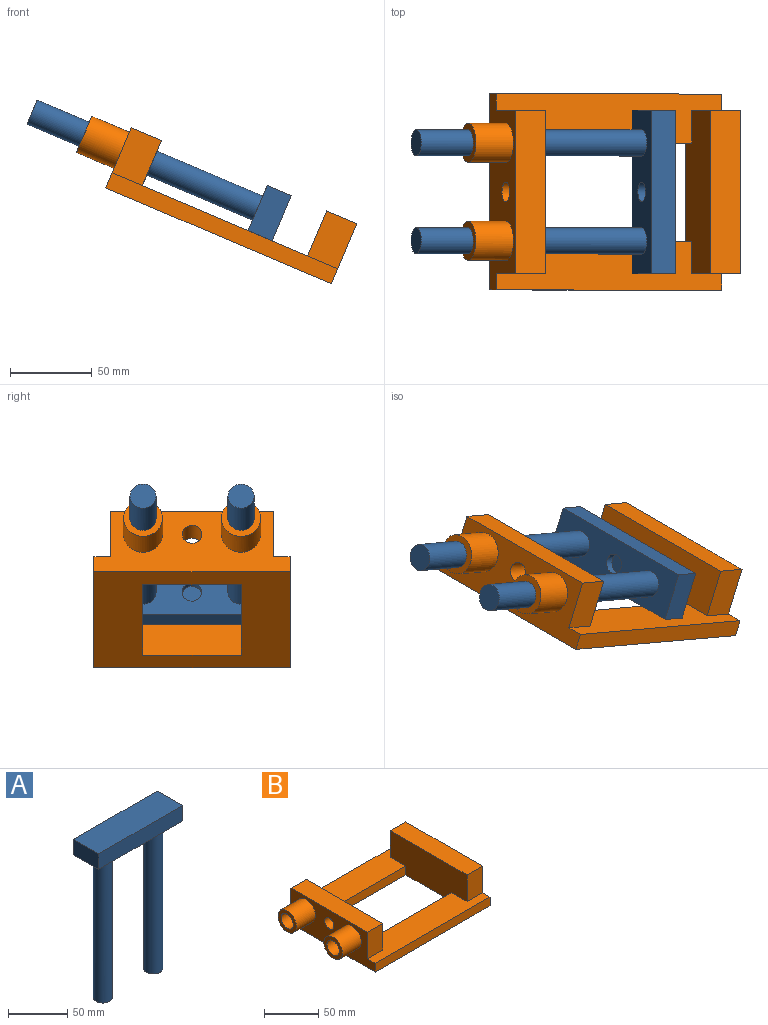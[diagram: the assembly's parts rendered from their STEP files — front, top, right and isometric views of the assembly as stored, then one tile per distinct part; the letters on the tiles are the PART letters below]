
ASSEMBLY  parts=2 mates=1
PART A: 12 faces, bbox 100x30x166 mm
  f0: plane 30x16mm, normal (1,0,0), area 480mm2, adj f1,f3,f4,f5
  f1: plane 100x16mm, normal (0,1,0), area 1600mm2, adj f0,f2,f4,f5
  f2: plane 30x16mm, normal (-1,0,0), area 480mm2, adj f1,f3,f4,f5
  f3: plane 100x16mm, normal (0,-1,0), area 1600mm2, adj f0,f2,f4,f5
  f4: plane 100x30mm, normal (0,0,1), area 3000mm2, adj f0,f1,f2,f3
  f5: plane 100x30mm, normal (0,0,-1), area 2484.8mm2, adj f0,f1,f2,f3,f6,f8,f10
  f6: cylinder r=8mm len=150mm, axis (0,0,1), area 7539.8mm2, adj f5,f7
  f7: plane 16x16mm, normal (0,0,-1), area 201.1mm2, adj f6
  f8: cylinder r=8mm len=150mm, axis (0,0,1), area 7539.8mm2, adj f5,f9
  f9: plane 16x16mm, normal (0,0,-1), area 201.1mm2, adj f8
  f10: cylinder r=6mm len=12mm, axis (0,0,-1), area 188.5mm2, adj f5,f11
  f11: plane 12x12mm, normal (0,0,-1), area 113.1mm2, adj f10
PART B: 24 faces, bbox 175x120x40 mm
  f0: plane 150x30mm, normal (0,0,1), area 3700mm2, adj f2,f3,f5,f6,f7,f9,f11,f15
  f1: plane 150x30mm, normal (0,0,1), area 3700mm2, adj f3,f4,f5,f7,f8,f9,f12,f14
  f2: plane 110x10mm, normal (0,-1,0), area 1100mm2, adj f0,f3,f9,f10
  f3: plane 100x40mm, normal (-1,0,0), area 3600mm2, adj f0,f1,f2,f4,f10,f11,f12,f13
  f4: plane 110x10mm, normal (0,1,0), area 1100mm2, adj f1,f3,f9,f10
  f5: plane 120x40mm, normal (1,0,0), area 4200mm2, adj f0,f1,f6,f8,f10,f11,f12,f13
  f6: plane 150x10mm, normal (0,1,0), area 1500mm2, adj f0,f5,f7,f10
  f7: plane 120x40mm, normal (-1,0,0), area 3182.1mm2, adj f0,f1,f6,f8,f10,f14,f15,f16
  f8: plane 150x10mm, normal (0,-1,0), area 1500mm2, adj f1,f5,f7,f10
  f9: plane 100x40mm, normal (1,0,0), area 3084.8mm2, adj f0,f1,f2,f4,f10,f14,f15,f16
  f10: plane 150x120mm, normal (0,0,-1), area 11400mm2, adj f2,f3,f4,f5,f6,f7,f8,f9
  f11: plane 30x20mm, normal (0,1,0), area 600mm2, adj f0,f3,f5,f13
  f12: plane 30x20mm, normal (0,-1,0), area 600mm2, adj f1,f3,f5,f13
  f13: plane 100x20mm, normal (0,0,1), area 2000mm2, adj f3,f5,f11,f12
  f14: plane 30x20mm, normal (0,-1,0), area 600mm2, adj f1,f7,f9,f16
  f15: plane 30x20mm, normal (0,1,0), area 600mm2, adj f0,f7,f9,f16
  f16: plane 100x20mm, normal (0,0,1), area 2000mm2, adj f7,f9,f14,f15
  f17: cylinder r=6mm len=20mm, axis (-1,0,0), area 754mm2, adj f7,f9
  f18: cylinder r=12mm len=25mm, axis (1,0,0), area 1885mm2, adj f7,f19
  f19: plane 24x24mm, normal (-1,0,0), area 251.3mm2, adj f18,f23
  f20: cylinder r=12mm len=25mm, axis (1,0,0), area 1885mm2, adj f7,f21
  f21: plane 24x24mm, normal (-1,0,0), area 251.3mm2, adj f20,f22
  f22: cylinder r=8mm len=45mm, axis (-1,0,0), area 2261.9mm2, adj f9,f21
  f23: cylinder r=8mm len=45mm, axis (-1,0,0), area 2261.9mm2, adj f9,f19
PLACE A rot(axis=(-0.64,0.64,-0.42),134.1deg) t=(31.89,-7.94,-21.48)mm
PLACE B rot(axis=(0,1,0),23deg) t=(7.93,-7.94,-38.46)mm
MATE slider A.f6 <-> B.f20  axis (-0.92,0,0.39) through (-106.15,-37.94,37.21)mm
